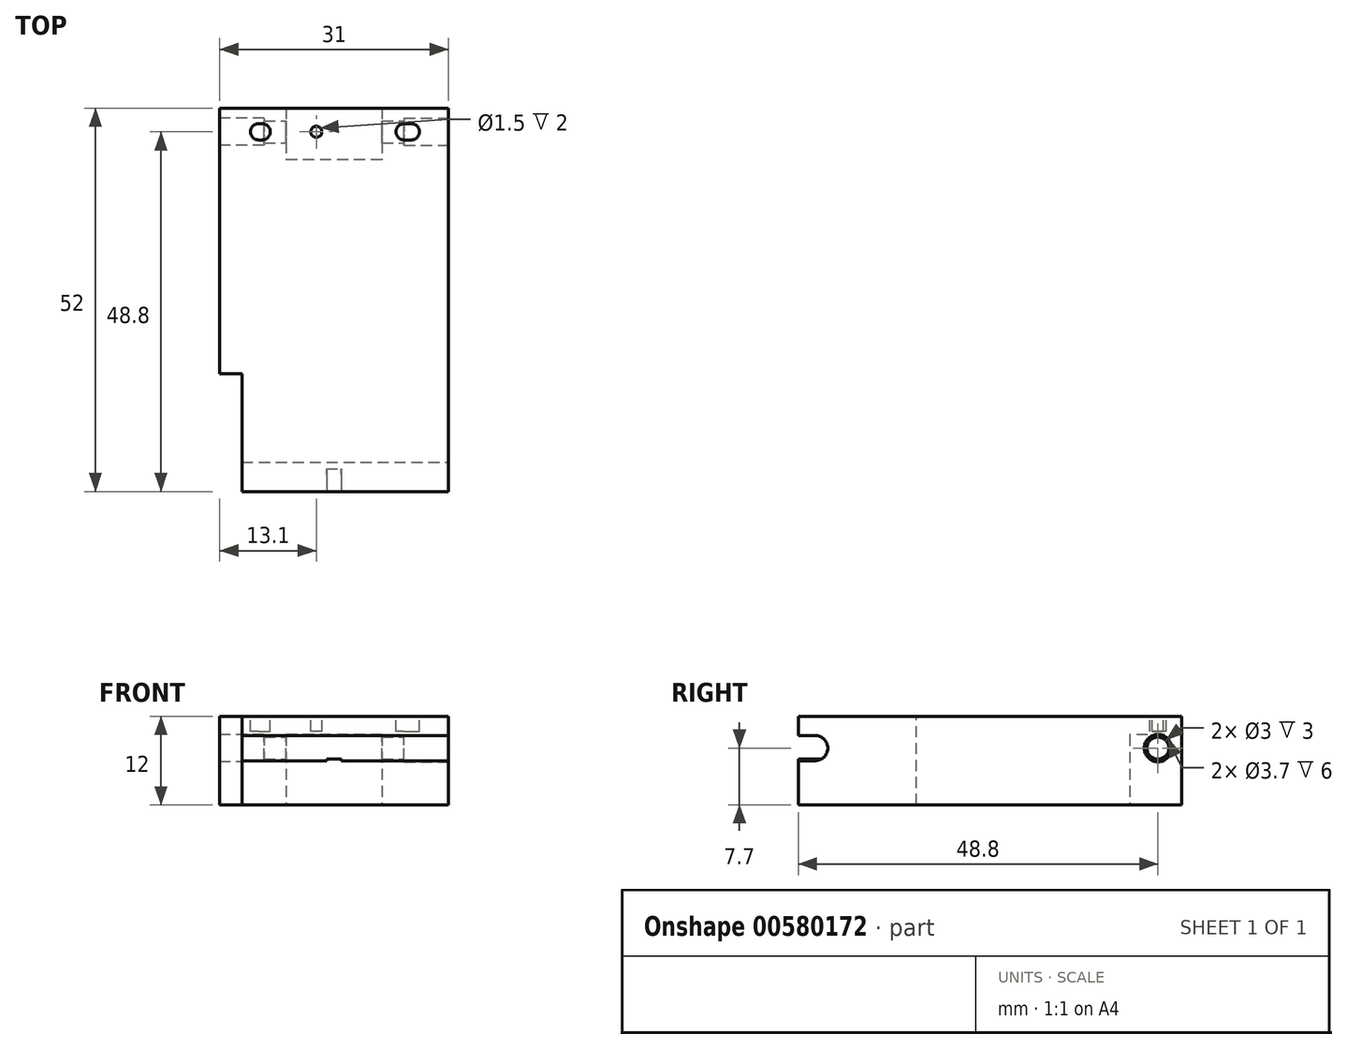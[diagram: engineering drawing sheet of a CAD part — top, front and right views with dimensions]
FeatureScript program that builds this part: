
annotation { "Feature Type Name" : "Feature", "Feature Type Description" : "" }
export const myFeature = defineFeature(function(context is Context, id is Id, definition is map)
    precondition{}
    {
        {
            var Q0;
            Q0=qCreatedBy(makeId("Top.planeOp"),FACE);
            var sketch = newSketch(context, id + "F0", { "sketchPlane" : qUnion([Q0])});
            skLineSegment(sketch, "E0.bottom", {"start": v(15.5, -26) * mm, "end": v(-15.5, -26) * mm});
            skLineSegment(sketch, "E0.top", {"start": v(15.5, 26) * mm, "end": v(-15.5, 26) * mm});
            skLineSegment(sketch, "E0.left", {"start": v(15.5, -26) * mm, "end": v(15.5, 26) * mm});
            skLineSegment(sketch, "E0.right", {"start": v(-15.5, -26) * mm, "end": v(-15.5, 26) * mm});
            skPoint(sketch, "E0.middle", {"position": v(0, 0) * mm});
            skSolve(sketch);
        }
        {
            var Q0;
            Q0=makeQuery(id+"F0.imprint","IMPRINT",FACE,{"disambiguationData":[TD([[makeQuery(id+"F0.imprint","IMPRINT",EDGE,{"derivedFrom":sQuery(id+"F0.wireOp",EDGE,"E0.bottom")}),-1.0]])]});
            extrude(context, id + "F1", {"entities" : qUnion([Q0]), "oppositeDirection" : true, "depth" : 12 * mm, "offsetDistance" : 25 * mm});
        }
        {
            var Q0;
            Q0=qCreatedBy(makeId("Right.planeOp"),FACE);
            var sketch = newSketch(context, id + "F2", { "sketchPlane" : qUnion([Q0])});
            skCircle(sketch, "E1", {"center": v(22.8, -4.3) * mm, "radius": 1.5 * mm});
            skArc(sketch, "E2", {"start": v(-23.7, -6) * mm, "mid": v(-22, -4.3) * mm, "end": v(-23.7, -2.6) * mm});
            skLineSegment(sketch, "E3", {"start": v(-23.7, -6) * mm, "end": v(-28.7, -6) * mm});
            skLineSegment(sketch, "E4", {"start": v(-23.7, -2.6) * mm, "end": v(-28.7, -2.6) * mm});
            skLineSegment(sketch, "E5", {"start": v(-28.7, -2.6) * mm, "end": v(-28.7, -6) * mm});
            skSolve(sketch);
        }
        {
            var Q0;
            Q0 = qSketchRegion(id + "F2", true);
            extrude(context, id + "F3", {"entities" : qUnion([Q0]), "operationType" : NewBodyOperationType.REMOVE, "endBound" : BoundingType.SYMMETRIC, "oppositeDirection" : true, "depth" : 50 * mm, "offsetDistance" : 25 * mm});
        }
        {
            var Q0;
            Q0=makeQuery(id+"F1.opExtrude","CAP_FACE",FACE,{"disambiguationData":[OSD([sQuery(id+"F0.wireOp",EDGE,"E0.bottom"),sQuery(id+"F0.wireOp",EDGE,"E0.top"),sQuery(id+"F0.wireOp",EDGE,"E0.left"),sQuery(id+"F0.wireOp",EDGE,"E0.right")])],"isStart":true});
            var sketch = newSketch(context, id + "F4", { "sketchPlane" : qUnion([Q0])});
            skArc(sketch, "E6", {"start": v(10.5, 21.7) * mm, "mid": v(11.6, 22.8) * mm, "end": v(10.5, 23.9) * mm});
            skLineSegment(sketch, "E7", {"start": v(10.5, 22.8) * mm, "end": v(-6.01, 22.8) * mm, "construction": true});
            skArc(sketch, "E8", {"start": v(9.5, 23.9) * mm, "mid": v(8.4, 22.8) * mm, "end": v(9.5, 21.7) * mm});
            skArc(sketch, "E9", {"start": v(-10.25, 23.9) * mm, "mid": v(-11.35, 22.8) * mm, "end": v(-10.25, 21.7) * mm});
            skLineSegment(sketch, "E10", {"start": v(-9.75, 21.7) * mm, "end": v(-10.25, 21.7) * mm});
            skLineSegment(sketch, "E11", {"start": v(-10.25, 23.9) * mm, "end": v(-9.75, 23.9) * mm});
            skLineSegment(sketch, "E12", {"start": v(9.5, 23.9) * mm, "end": v(10.5, 23.9) * mm});
            skLineSegment(sketch, "E13", {"start": v(10.5, 21.7) * mm, "end": v(9.5, 21.7) * mm});
            skArc(sketch, "E14.trimOffspring", {"start": v(-9.75, 21.7) * mm, "mid": v(-8.65, 22.8) * mm, "end": v(-9.75, 23.9) * mm});
            skPoint(sketch, "E15", {"position": v(-10, 21.7) * mm});
            skPoint(sketch, "E16", {"position": v(10, 21.7) * mm});
            skCircle(sketch, "E17", {"center": v(-2.4, 22.8) * mm, "radius": 0.75 * mm});
            skSolve(sketch);
        }
        {
            var Q0;
            Q0 = qSketchRegion(id + "F4", true);
            extrude(context, id + "F5", {"entities" : qUnion([Q0]), "operationType" : NewBodyOperationType.REMOVE, "oppositeDirection" : true, "depth" : 2 * mm, "offsetDistance" : 25 * mm});
        }
        {
            var Q0;
            {var subQ2=sQuery(id+"F0.wireOp",EDGE,"E0.bottom");Q0=makeQuery(id+"F3.boolean.opBoolean","SPLIT",FACE,{"disambiguationData":[TD([makeQuery(id+"F3.opExtrude","SWEPT_FACE",FACE,{"disambiguationData":[OSD([sQuery(id+"F2.wireOp",EDGE,"E3")])]})])],"derivedFrom":makeQuery(id+"F1.opExtrude","SWEPT_FACE",FACE,{"disambiguationData":[OSD([subQ2])]})});}
            var sketch = newSketch(context, id + "F6", { "sketchPlane" : qUnion([Q0])});
            skLineSegment(sketch, "E18.bottom", {"start": v(-1, -6) * mm, "end": v(1, -6) * mm});
            skLineSegment(sketch, "E18.top", {"start": v(-1, -5.8) * mm, "end": v(1, -5.8) * mm});
            skLineSegment(sketch, "E18.left", {"start": v(-1, -6) * mm, "end": v(-1, -5.8) * mm});
            skLineSegment(sketch, "E18.right", {"start": v(1, -6) * mm, "end": v(1, -5.8) * mm});
            skSolve(sketch);
        }
        {
            var Q0;
            Q0 = qSketchRegion(id + "F6", true);
            extrude(context, id + "F7", {"entities" : qUnion([Q0]), "operationType" : NewBodyOperationType.ADD, "endBound" : BoundingType.UP_TO_NEXT, "oppositeDirection" : true, "depth" : 25 * mm, "offsetDistance" : 25 * mm});
        }
        {
            var Q0;
            Q0=makeQuery(id+"F1.opExtrude","CAP_FACE",FACE,{"disambiguationData":[OSD([sQuery(id+"F0.wireOp",EDGE,"E0.bottom"),sQuery(id+"F0.wireOp",EDGE,"E0.top"),sQuery(id+"F0.wireOp",EDGE,"E0.left"),sQuery(id+"F0.wireOp",EDGE,"E0.right")])],"isStart":true});
            var sketch = newSketch(context, id + "F8", { "sketchPlane" : qUnion([Q0])});
            skLineSegment(sketch, "E19.bottom", {"start": v(-15.5, -26) * mm, "end": v(-12.5, -26) * mm});
            skLineSegment(sketch, "E19.top", {"start": v(-15.5, -10) * mm, "end": v(-12.5, -10) * mm});
            skLineSegment(sketch, "E19.left", {"start": v(-15.5, -26) * mm, "end": v(-15.5, -10) * mm});
            skLineSegment(sketch, "E19.right", {"start": v(-12.5, -26) * mm, "end": v(-12.5, -10) * mm});
            skSolve(sketch);
        }
        {
            var Q0;
            Q0 = qSketchRegion(id + "F8", true);
            extrude(context, id + "F9", {"entities" : qUnion([Q0]), "operationType" : NewBodyOperationType.REMOVE, "endBound" : BoundingType.THROUGH_ALL, "oppositeDirection" : true, "depth" : 25 * mm, "offsetDistance" : 25 * mm});
        }
        {
            var Q0;
            Q0=makeQuery(id+"F1.opExtrude","CAP_FACE",FACE,{"disambiguationData":[OSD([sQuery(id+"F0.wireOp",EDGE,"E0.bottom"),sQuery(id+"F0.wireOp",EDGE,"E0.top"),sQuery(id+"F0.wireOp",EDGE,"E0.left"),sQuery(id+"F0.wireOp",EDGE,"E0.right")])],"isStart":false});
            var sketch = newSketch(context, id + "F10", { "sketchPlane" : qUnion([Q0])});
            skLineSegment(sketch, "E20.bottom", {"start": v(6.5, -26) * mm, "end": v(-6.5, -26) * mm});
            skLineSegment(sketch, "E20.top", {"start": v(6.5, -19) * mm, "end": v(-6.5, -19) * mm});
            skLineSegment(sketch, "E20.left", {"start": v(6.5, -26) * mm, "end": v(6.5, -19) * mm});
            skLineSegment(sketch, "E20.right", {"start": v(-6.5, -26) * mm, "end": v(-6.5, -19) * mm});
            skSolve(sketch);
        }
        {
            var Q0;
            Q0 = qSketchRegion(id + "F10", true);
            extrude(context, id + "F11", {"entities" : qUnion([Q0]), "operationType" : NewBodyOperationType.REMOVE, "oppositeDirection" : true, "depth" : 9.5 * mm, "offsetDistance" : 25 * mm});
        }
        {
            var Q0;
            Q0=makeQuery(id+"F1.opExtrude","SWEPT_FACE",FACE,{"disambiguationData":[OSD([sQuery(id+"F0.wireOp",EDGE,"E0.right")])]});
            var sketch = newSketch(context, id + "F12", { "sketchPlane" : qUnion([Q0])});
            skCircle(sketch, "E21", {"center": v(-22.8, -4.3) * mm, "radius": 1.85 * mm});
            skSolve(sketch);
        }
        {
            var Q0;
            Q0=makeQuery(id+"F12.imprint","IMPRINT",FACE,{"disambiguationData":[TD([[makeQuery(id+"F12.imprint","IMPRINT",EDGE,{"derivedFrom":sQuery(id+"F12.wireOp",EDGE,"E21")}),1.0]])]});
            var Q1;
            Q1=sQuery(id+"F12.wireOp",EDGE,"E21");
            extrude(context, id + "F13", {"entities" : qUnion([Q0]), "operationType" : NewBodyOperationType.REMOVE, "surfaceEntities" : qUnion([Q1]), "oppositeDirection" : true, "depth" : 6 * mm, "offsetDistance" : 25 * mm});
        }
        {
            var Q0;
            Q0=makeQuery(id+"F1.opExtrude","SWEPT_FACE",FACE,{"disambiguationData":[OSD([sQuery(id+"F0.wireOp",EDGE,"E0.left")])]});
            var sketch = newSketch(context, id + "F14", { "sketchPlane" : qUnion([Q0])});
            skCircle(sketch, "E22", {"center": v(22.8, -4.3) * mm, "radius": 1.85 * mm});
            skSolve(sketch);
        }
        {
            var Q0;
            Q0 = qSketchRegion(id + "F14", true);
            extrude(context, id + "F15", {"entities" : qUnion([Q0]), "operationType" : NewBodyOperationType.REMOVE, "oppositeDirection" : true, "depth" : 6 * mm, "offsetDistance" : 25 * mm});
        }
    });
